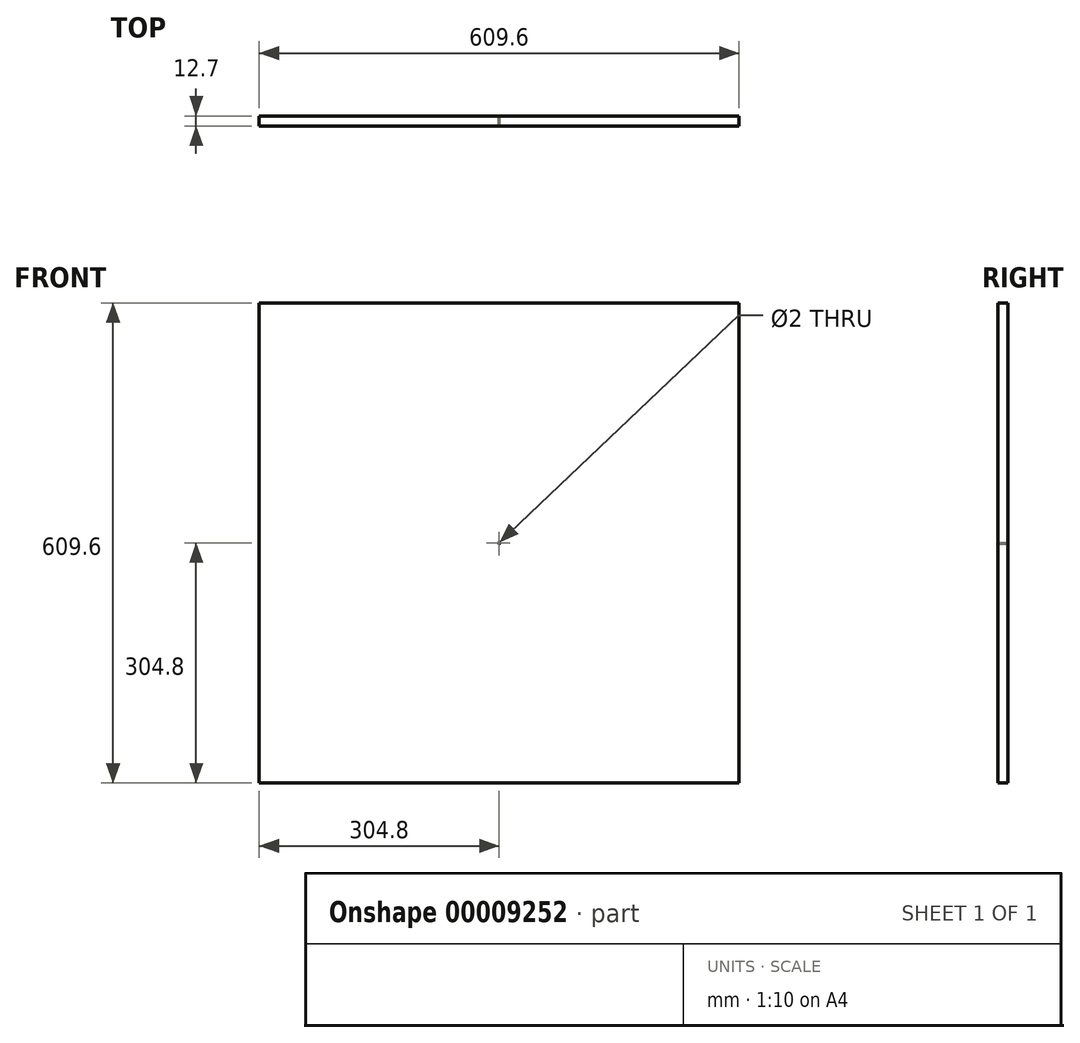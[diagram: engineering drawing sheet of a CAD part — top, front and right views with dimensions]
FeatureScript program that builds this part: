
annotation { "Feature Type Name" : "Feature", "Feature Type Description" : "" }
export const myFeature = defineFeature(function(context is Context, id is Id, definition is map)
    precondition{}
    {
        {
            var Q0;
            Q0=qCreatedBy(makeId("Front.planeOp"),FACE);
            var sketch = newSketch(context, id + "F0", { "sketchPlane" : qUnion([Q0])});
            skLineSegment(sketch, "E0.rect.bottom", {"start": v(304.8, 304.8) * mm, "end": v(-304.8, 304.8) * mm});
            skLineSegment(sketch, "E0.rect.top", {"start": v(304.8, -304.8) * mm, "end": v(-304.8, -304.8) * mm});
            skLineSegment(sketch, "E0.rect.left", {"start": v(304.8, 304.8) * mm, "end": v(304.8, -304.8) * mm});
            skLineSegment(sketch, "E0.rect.right", {"start": v(-304.8, 304.8) * mm, "end": v(-304.8, -304.8) * mm});
            skPoint(sketch, "E0.rect.middle", {"position": v(0, 0) * mm});
            skCircle(sketch, "E1", {"center": v(0, 0) * mm, "radius": 1 * mm});
            skSolve(sketch);
        }
        {
            var Q0;
            Q0=makeQuery(id+"F0.imprint","IMPRINT",FACE,{"disambiguationData":[TD([[makeQuery(id+"F0.imprint","IMPRINT",EDGE,{"derivedFrom":sQuery(id+"F0.wireOp",EDGE,"E0.rect.bottom")}),1.0]])]});
            extrude(context, id + "F1", {"entities" : qUnion([Q0]), "depth" : 12.7 * mm});
        }
    });
